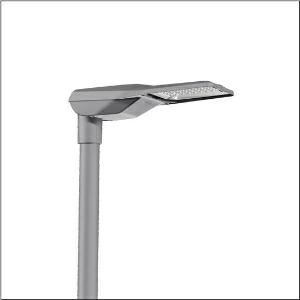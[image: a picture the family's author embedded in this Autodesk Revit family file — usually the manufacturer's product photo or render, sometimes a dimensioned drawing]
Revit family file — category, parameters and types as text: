
# Revit family: streetlight_sl_21_mini___stw1_0a_5xe6e63a08hb_69e0
name_source: partatom
category: Lighting Fixtures
units: mm (PartAtom-declared; Revit-internal decimal feet)

## family parameters
Cut with Voids When Loaded = No
Host = Face
Light Source = No
Part Type = Normal
Room Calculation Point = No
Round Connector Dimension = Use Diameter
Shared = No

## types (1)
- --- (1 x LED, 8110 lm, 66 W, 2700K)
    Apparent Load = 66 VA
    CIE Flux Codes = 38 75 98 100 100
    Color Rendering = 70
    Color Temperature = 2700K
    Default Elevation = 1800 mm
    Description = Streetlight SL 21 mini, mast luminaire, primary light control with lens, of PMMA, primary optical cover: cover, of toughened safety glass, transparent, light distribution: STW1.0a, light emission: direct distribution, primary light characteristic: asymmetric, installation type: post-top, side-entry, LED, 3G 1.5mm², High Power LED, rated luminous flux: 8.110lm, luminous efficacy: 123lm/W, light colour: 727, colour temperature: 2700K, control: overheat protection, constant luminous flux control, time-dependent luminous flux control, flexible luminous flux parameterisation, mains connection: 230..240V, AC, 50/60Hz, connection cable pre-assembled, cable length: 8,5m, wiring characteristics: H07RN-F, start of lifetime: 66W, end of service life: 69W, reduction: 30W, luminaire housing, of diecast aluminium, powder-coated, Siteco® metallic grey (DB 702S), corrosivity category C5 mid according to DIN EN ISO 12944, please order mast flange separately, inclination adjustable: 0°, 5°, 10°, 15°, sealing non-destructively replaceable, multi-level sealing system, length: 628mm, width: 235mm, height: 110mm, mast flange for spigot size: 42mm (side-entry): 5XC10008XM4, 60/48mm (side-entry/post-top): 5XC10108XM2, 76/60mm (side-entry/post-top): 5XC10108XM1, protection rating (complete): IP66, insulation class (complete): insulation class II (safety insulation), certification: CE, ENEC, ENEC+, VDE, impact resistance: IK09, permissible operating ambient temperature for outdoor applications: -40..+50°C, standard-compliant lighting for roads and squares, packaging unit: 1 piece

Light Distribution: STW1.0a
    Height = 110 mm
    Lamp = 1 x LED
    Lamp Light Flux = 8110 lm
    Lamp Power = 66 W
    Lamp count = 1
    Length = 625 mm
    Luminous efficacy = 123 lm/W
    Manufacturer = Siteco
    ModVariant = No
    Model = 5XE6E63A08HB
    Number of Poles = 1
    OnlyDefault = Yes
    Power Factor = 1
    Product Name = Streetlight SL 21 mini | STW1.0a
    Product group = mast luminaire | pylon top
    ProductGroupID = 6100
    Protection Class = Protection class II
    Protection Degree = IP 66
    RLX_Detail_Level = 1
    RLX_Emergency_Light_Flux = 0 lm
    RLX_Emergency_Type = 0
    RLX_Emergency_Type_DB = No
    RlxData = <blob elided: 92113 chars, md5=06e4e7ff>
    Socket = socket
    Standby Power = 0 W
    System Light Flux = 8110 lm
    System Power = 66 W
    Type Comments = factory setting: luminous flux: 100 % | Output Level: 100 % | 670 mA
    Type Image = l_1003519.jpg
    URL = http://relux.com
    VarID = @adj_120389
    Voltage = 0 V
    Weight = 0.00 kg
    Width = 234 mm

## geometry (parser evidence)
native form markers: Blend x4, Sweep x13
no freeform markers — native parametric forms only
